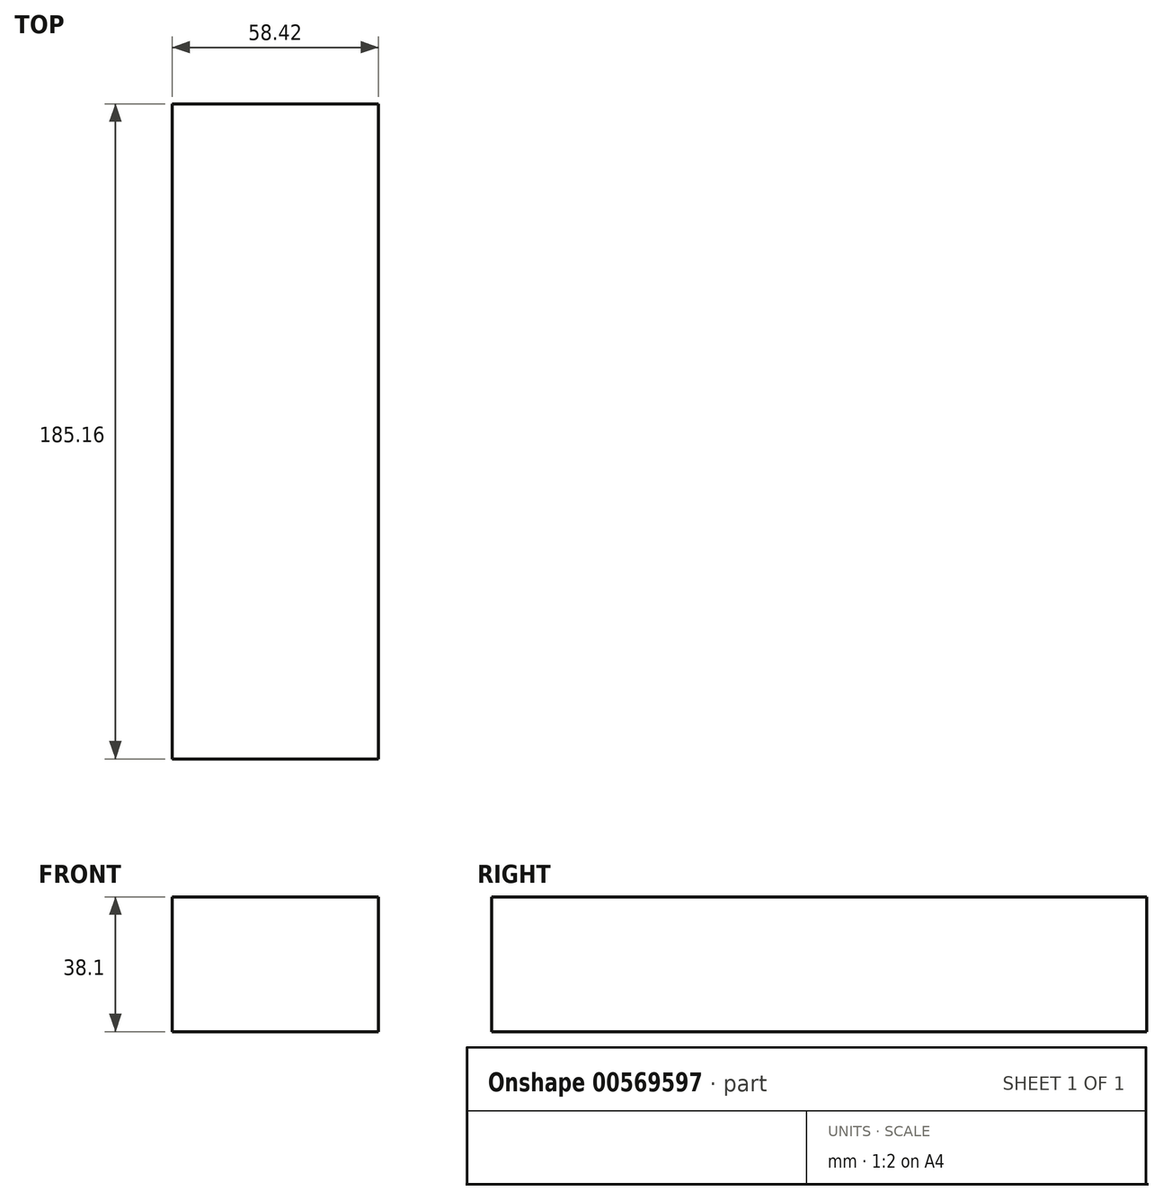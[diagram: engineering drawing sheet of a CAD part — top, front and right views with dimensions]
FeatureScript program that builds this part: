
annotation { "Feature Type Name" : "Feature", "Feature Type Description" : "" }
export const myFeature = defineFeature(function(context is Context, id is Id, definition is map)
    precondition{}
    {
        {
            var Q0;
            Q0=qCreatedBy(makeId("Top.planeOp"),FACE);
            var sketch = newSketch(context, id + "F0", { "sketchPlane" : qUnion([Q0])});
            skLineSegment(sketch, "E0.bottom", {"start": v(29.2, -92.58) * mm, "end": v(-29.21, -92.58) * mm});
            skLineSegment(sketch, "E0.top", {"start": v(29.21, 92.58) * mm, "end": v(-29.2, 92.58) * mm});
            skLineSegment(sketch, "E0.left", {"start": v(29.2, -92.58) * mm, "end": v(29.21, 92.58) * mm});
            skLineSegment(sketch, "E0.right", {"start": v(-29.21, -92.58) * mm, "end": v(-29.2, 92.58) * mm});
            skPoint(sketch, "E0.middle", {"position": v(0, 0) * mm});
            skSolve(sketch);
        }
        {
            var Q0;
            Q0 = qSketchRegion(id + "F0", true);
            extrude(context, id + "F1", {"entities" : qUnion([Q0]), "depth" : 38.1 * mm, "offsetDistance" : 25.4 * mm});
        }
    });
